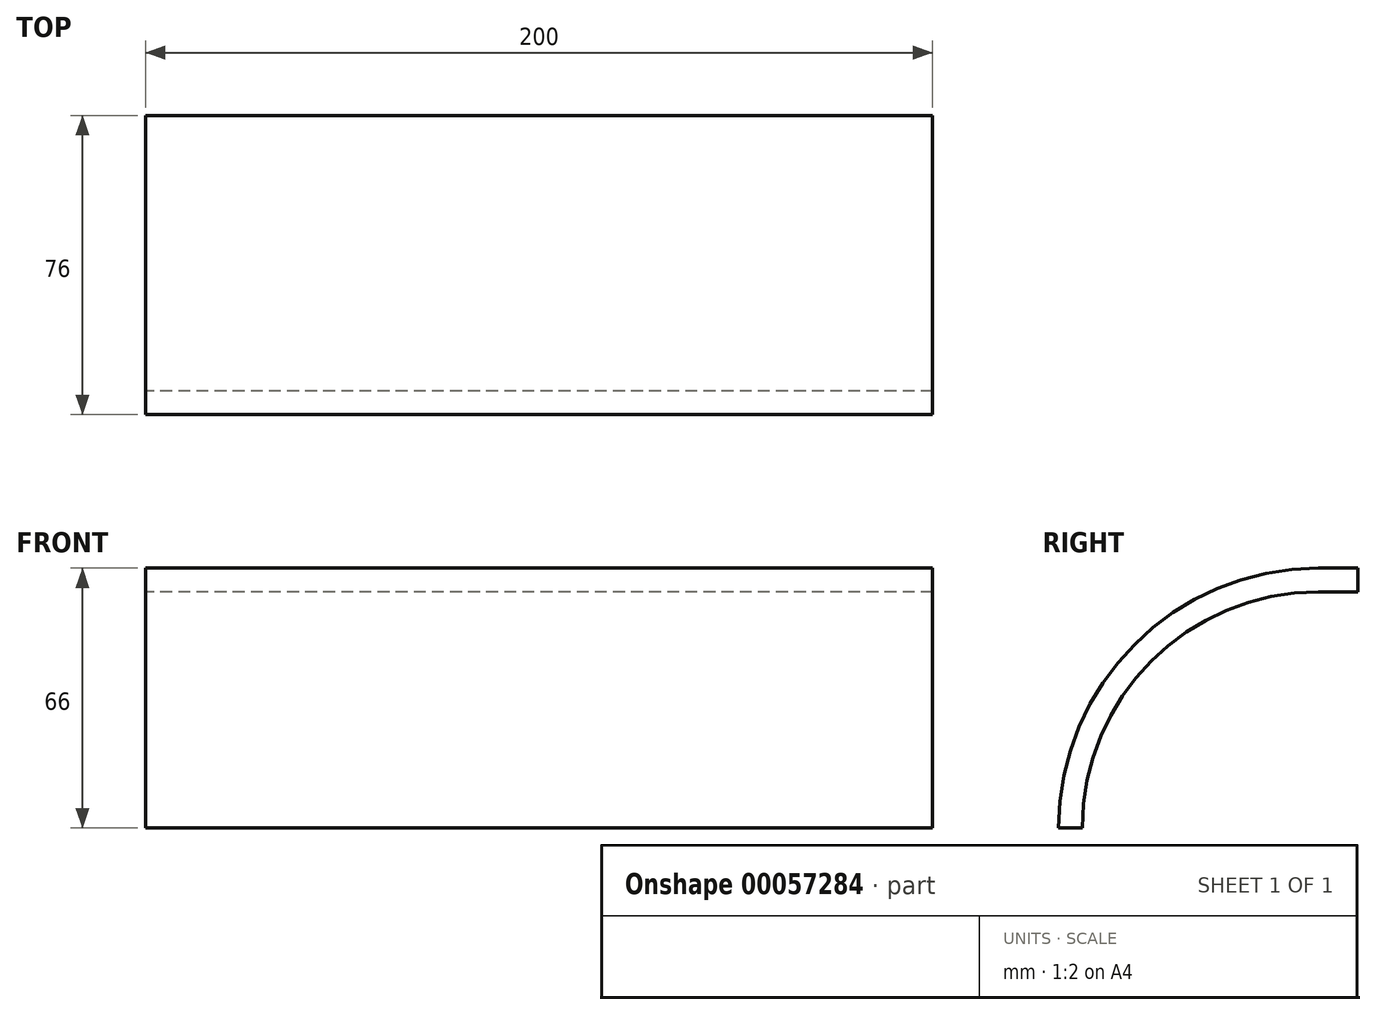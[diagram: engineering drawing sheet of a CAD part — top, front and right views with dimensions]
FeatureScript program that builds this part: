
annotation { "Feature Type Name" : "Feature", "Feature Type Description" : "" }
export const myFeature = defineFeature(function(context is Context, id is Id, definition is map)
    precondition{}
    {
        {
            var Q0;
            Q0=qCreatedBy(makeId("Right.planeOp"),FACE);
            var sketch = newSketch(context, id + "F0", { "sketchPlane" : qUnion([Q0])});
            skLineSegment(sketch, "E0", {"start": v(0, 60) * mm, "end": v(0, 66) * mm, "construction": true});
            skLineSegment(sketch, "E1", {"start": v(0, 66) * mm, "end": v(0, 60) * mm, "construction": true});
            skLineSegment(sketch, "E2", {"start": v(-70, 0) * mm, "end": v(-76, 0) * mm});
            skLineSegment(sketch, "E3.0", {"start": v(-10, 66) * mm, "end": v(-10, 60) * mm});
            skArc(sketch, "E4", {"start": v(-10, 60) * mm, "mid": v(-52.43, 42.43) * mm, "end": v(-70, 0) * mm});
            skLineSegment(sketch, "E5", {"start": v(-10, 60) * mm, "end": v(0, 60) * mm});
            skArc(sketch, "E6.0", {"start": v(-10, 66) * mm, "mid": v(-56.67, 46.67) * mm, "end": v(-76, 0) * mm});
            skLineSegment(sketch, "E7.0", {"start": v(-10, 66) * mm, "end": v(0, 66) * mm});
            skLineSegment(sketch, "E8", {"start": v(0, 66) * mm, "end": v(0, 60) * mm});
            skSolve(sketch);
        }
        {
            var Q0;
            Q0=makeQuery(id+"F0.imprint","IMPRINT",FACE,{"disambiguationData":[TD([[makeQuery(id+"F0.imprint","IMPRINT",EDGE,{"derivedFrom":sQuery(id+"F0.wireOp",EDGE,"E3.0")}),-1.0]])]});
            var Q1;
            Q1=makeQuery(id+"F0.imprint","IMPRINT",FACE,{"disambiguationData":[TD([[makeQuery(id+"F0.imprint","IMPRINT",EDGE,{"derivedFrom":sQuery(id+"F0.wireOp",EDGE,"E3.0")}),1.0]])]});
            extrude(context, id + "F1", {"entities" : qUnion([Q0, Q1]), "depth" : 200 * mm});
        }
    });
